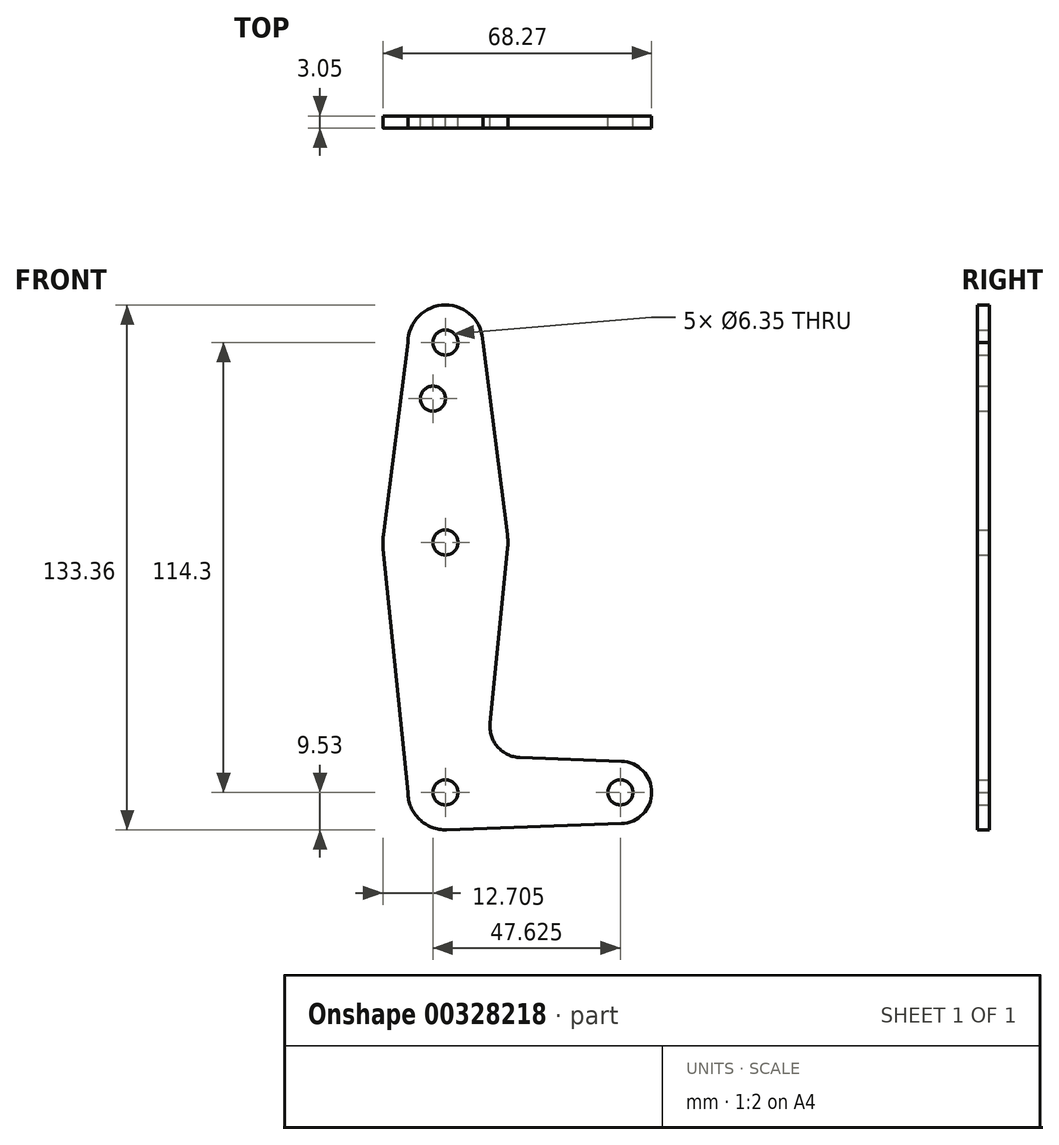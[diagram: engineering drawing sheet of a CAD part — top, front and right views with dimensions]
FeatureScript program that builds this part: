
annotation { "Feature Type Name" : "Feature", "Feature Type Description" : "" }
export const myFeature = defineFeature(function(context is Context, id is Id, definition is map)
    precondition{}
    {
        {
            var Q0;
            Q0=qCreatedBy(makeId("Front.planeOp"),FACE);
            var sketch = newSketch(context, id + "F0", { "sketchPlane" : qUnion([Q0])});
            skLineSegment(sketch, "E0", {"start": v(0, 0) * mm, "end": v(0, 114.3) * mm, "construction": true});
            skLineSegment(sketch, "E1", {"start": v(0, 0) * mm, "end": v(44.45, 0) * mm, "construction": true});
            skCircle(sketch, "E2", {"center": v(0, 114.3) * mm, "radius": 9.53 * mm});
            skCircle(sketch, "E3", {"center": v(0, 63.5) * mm, "radius": 15.88 * mm});
            skCircle(sketch, "E4", {"center": v(0, 0) * mm, "radius": 9.53 * mm});
            skCircle(sketch, "E5", {"center": v(44.45, 0) * mm, "radius": 7.94 * mm});
            skLineSegment(sketch, "E6", {"start": v(0.34, -9.52) * mm, "end": v(44.73, -7.93) * mm});
            skLineSegment(sketch, "E7", {"start": v(-9.52, 114.3) * mm, "end": v(-15.75, 65.5) * mm});
            skLineSegment(sketch, "E8", {"start": v(9.52, 114.3) * mm, "end": v(15.75, 65.5) * mm});
            skLineSegment(sketch, "E9", {"start": v(-15.8, 61.9) * mm, "end": v(-9.52, 0) * mm});
            skCircle(sketch, "E10", {"center": v(0, 114.3) * mm, "radius": 3.18 * mm});
            skCircle(sketch, "E11", {"center": v(0, 63.5) * mm, "radius": 3.18 * mm});
            skCircle(sketch, "E12", {"center": v(0, 0) * mm, "radius": 3.18 * mm});
            skCircle(sketch, "E13", {"center": v(44.45, 0) * mm, "radius": 3.18 * mm});
            skLineSegment(sketch, "E14", {"start": v(15.8, 61.91) * mm, "end": v(11.34, 17.6) * mm});
            skLineSegment(sketch, "E15", {"start": v(18.97, 8.85) * mm, "end": v(44.73, 7.93) * mm});
            skArc(sketch, "E16.filletArc", {"start": v(11.34, 17.6) * mm, "mid": v(13.26, 11.57) * mm, "end": v(18.97, 8.85) * mm});
            skCircle(sketch, "E17", {"center": v(-3.18, 100.03) * mm, "radius": 3.18 * mm});
            skSolve(sketch);
        }
        {
            var Q0;
            Q0 = qSketchRegion(id + "F0", true);
            extrude(context, id + "F1", {"entities" : qUnion([Q0]), "depth" : 3.05 * mm});
        }
    });
